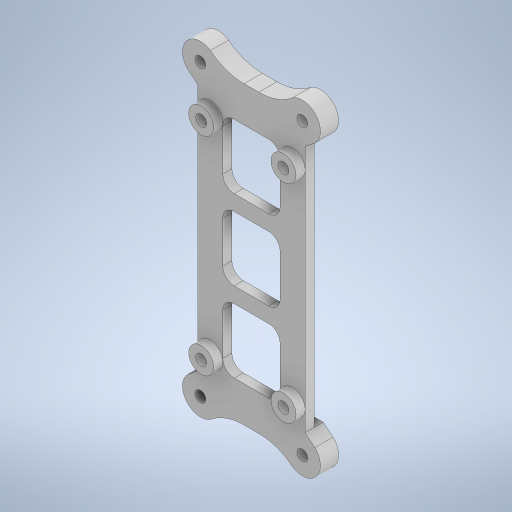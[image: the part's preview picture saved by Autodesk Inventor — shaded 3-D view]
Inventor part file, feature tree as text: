
AUTODESK INVENTOR PART (.ipt)
format: ipt  version: 2023 (Build 270158000, 158)  size: 441,344 bytes
history: native  units: in
note: dims shown in document units (in); Inventor stores cm internally (conversion verified against a paired STEP export)
features: extrude x4, sketch x4, other x3, reference x2, projected_geometry x1
ambient origin geometry x8: Origin, YZ Plane, XZ Plane, XY Plane, X Axis, Y Axis, Z Axis, Center Point
bodies: Solid1 (feature_tree)
feature tree (14):
  extrude  "Extrusion1"  Depth=0.2756in
  extrude  "Extrusion2"  Depth=0.1772in
  extrude  "Extrusion3"  Depth=0.125in
  extrude  "Extrusion4"  Depth=0.1in TaperAngle=0.0deg
  sketch  "Sketch1"  dims[d0=0.2756in d1=0.2756in]
  reference  "Reference1"
  reference  "Reference2"
  sketch  "Sketch2"  dims[d2=2.9in d5=0.1772in]
  sketch  "Sketch3"  dims[d6=0.1772in d9=0.125in]
  sketch  "Sketch4"  dims[d10=0.125in d11=0.1in d12=0.0in d13=0.2756in d14=2.2835in d15=0.9055in d16=1.1811in d17=0.5906in d18=0.2756in d19=0.2756in d20=0.2756in d22=0.9055in d23=2.2835in d24=0.4528in d27=0.4854in d29=0.4854in d30=0.1in d31=0.0in d32=0.7087in d33=0.7087in d34=0.7087in d35=0.1705in d36=0.1705in d37=0.125in d38=0.1181in d39=0.1181in d40=0.1181in d41=0.1181in d42=0.1in d43=0.0in d44=0.1in d45=0.0in]
  projected_geometry  "Projected Loop1"
  parser-record x1  (decoder bookkeeping rows leaked as tree rows — omitted from the tree; the rows remain in map.json)
  other  "ECE477.iam"
  other  "Source Two v0.1_import:1"
note: 1 file-system path scrubbed to <path> (originals preserved in map.json)
